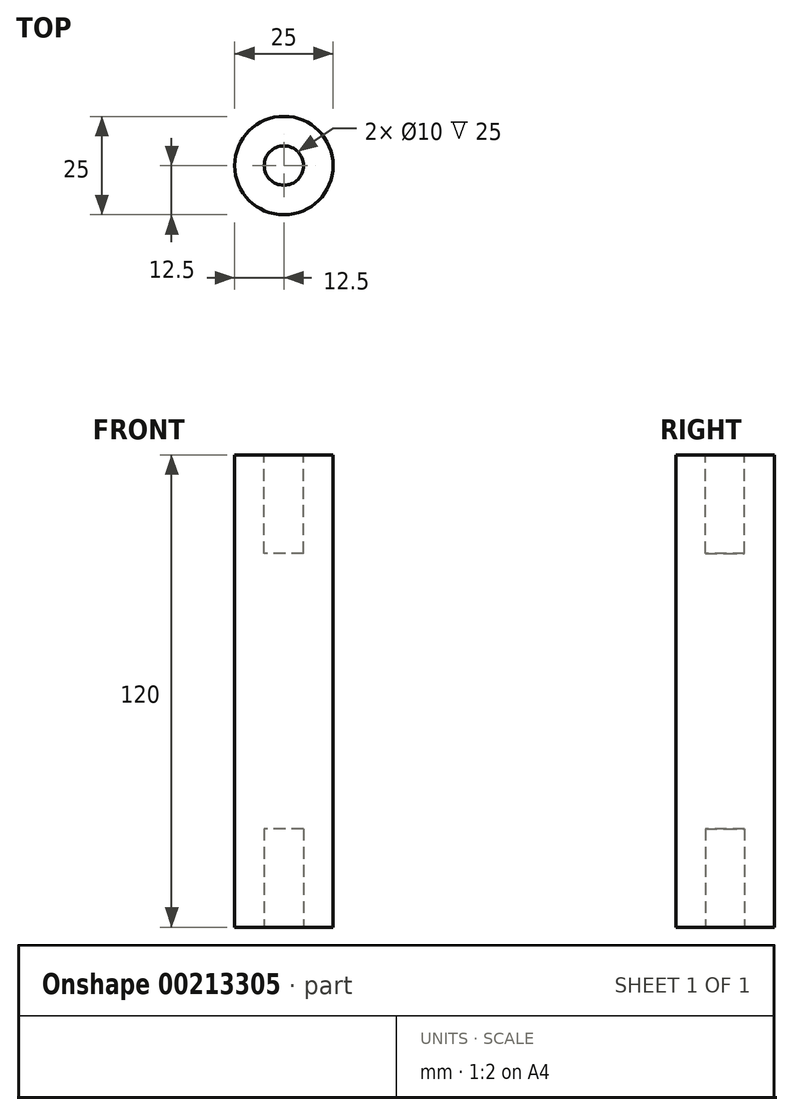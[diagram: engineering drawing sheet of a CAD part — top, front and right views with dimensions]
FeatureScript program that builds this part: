
annotation { "Feature Type Name" : "Feature", "Feature Type Description" : "" }
export const myFeature = defineFeature(function(context is Context, id is Id, definition is map)
    precondition{}
    {
        {
            var Q0;
            Q0=qCreatedBy(makeId("Top.planeOp"),FACE);
            var sketch = newSketch(context, id + "F0", { "sketchPlane" : qUnion([Q0])});
            skCircle(sketch, "E0", {"center": v(0, 0) * mm, "radius": 12.5 * mm});
            skCircle(sketch, "E1", {"center": v(0, 0) * mm, "radius": 5 * mm});
            skSolve(sketch);
        }
        {
            var Q0;
            Q0=makeQuery(id+"F0.imprint","IMPRINT",FACE,{"disambiguationData":[TD([[makeQuery(id+"F0.imprint","IMPRINT",EDGE,{"derivedFrom":sQuery(id+"F0.wireOp",EDGE,"E0")}),1.0]])]});
            var Q1;
            Q1=makeQuery(id+"F0.imprint","IMPRINT",FACE,{"disambiguationData":[TD([[makeQuery(id+"F0.imprint","IMPRINT",EDGE,{"derivedFrom":sQuery(id+"F0.wireOp",EDGE,"E1")}),1.0]])]});
            extrude(context, id + "F1", {"entities" : qUnion([Q0, Q1]), "oppositeDirection" : true, "depth" : (120 / 2) * mm});
        }
        {
            var Q0;
            Q0=makeQuery(id+"F0.imprint","IMPRINT",FACE,{"disambiguationData":[TD([[makeQuery(id+"F0.imprint","IMPRINT",EDGE,{"derivedFrom":sQuery(id+"F0.wireOp",EDGE,"E1")}),1.0]])]});
            extrude(context, id + "F2", {"entities" : qUnion([Q0]), "operationType" : NewBodyOperationType.REMOVE, "oppositeDirection" : true, "depth" : 25 * mm});
        }
        {
            var Q0;
            Q0=makeQuery(id+"F1.opExtrude","SWEPT_BODY",BODY,{"disambiguationData":[OSD([sQuery(id+"F0.wireOp",EDGE,"E0")])]});
            var Q1;
            Q1=makeQuery(id+"F1.opExtrude","CAP_FACE",FACE,{"disambiguationData":[OSD([sQuery(id+"F0.wireOp",EDGE,"E0")])],"isStart":false});
            mirror(context, id + "F3", {"operationType" : NewBodyOperationType.ADD, "entities" : qUnion([Q0]), "mirrorPlane" : qUnion([Q1])});
        }
    });
